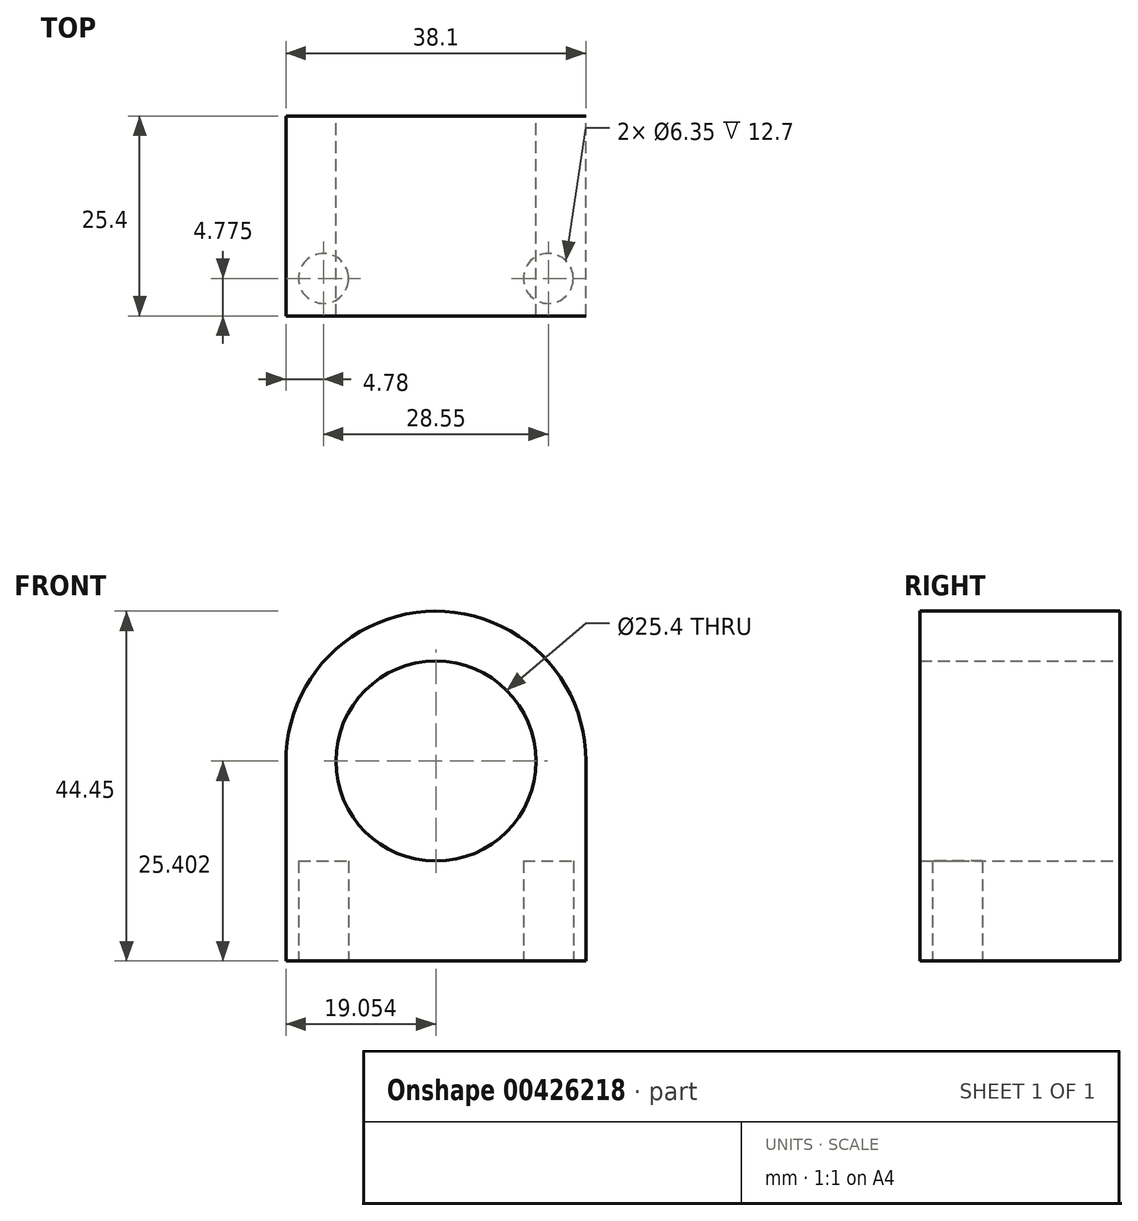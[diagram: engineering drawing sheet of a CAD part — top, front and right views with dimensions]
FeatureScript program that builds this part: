
annotation { "Feature Type Name" : "Feature", "Feature Type Description" : "" }
export const myFeature = defineFeature(function(context is Context, id is Id, definition is map)
    precondition{}
    {
        {
            var Q0;
            Q0=qCreatedBy(makeId("Front.planeOp"),FACE);
            var sketch = newSketch(context, id + "F0", { "sketchPlane" : qUnion([Q0])});
            skArc(sketch, "E0", {"start": v(4.83, 30.33) * mm, "mid": v(-14.3, 49.38) * mm, "end": v(-33.27, 30.17) * mm});
            skCircle(sketch, "E1", {"center": v(-14.22, 30.33) * mm, "radius": 12.7 * mm});
            skLineSegment(sketch, "E2", {"start": v(-33.27, 30.5) * mm, "end": v(-33.27, 4.93) * mm});
            skLineSegment(sketch, "E3", {"start": v(-33.27, 4.93) * mm, "end": v(4.83, 4.93) * mm});
            skLineSegment(sketch, "E4", {"start": v(4.83, 4.93) * mm, "end": v(4.83, 30.33) * mm});
            skSolve(sketch);
        }
        {
            var Q0;
            Q0 = qSketchRegion(id + "F0", true);
            extrude(context, id + "F1", {"entities" : qUnion([Q0]), "depth" : 25.4 * mm});
        }
        {
            var Q0;
            Q0=makeQuery(id+"F1.opExtrude","SWEPT_FACE",FACE,{"disambiguationData":[OSD([sQuery(id+"F0.wireOp",EDGE,"E3")])]});
            var sketch = newSketch(context, id + "F2", { "sketchPlane" : qUnion([Q0])});
            skCircle(sketch, "E5", {"center": v(-28.5, 20.62) * mm, "radius": 3.18 * mm});
            skCircle(sketch, "E6", {"center": v(0.06, 20.62) * mm, "radius": 3.18 * mm});
            skSolve(sketch);
        }
        {
            var Q0;
            Q0 = qSketchRegion(id + "F2", true);
            extrude(context, id + "F3", {"entities" : qUnion([Q0]), "operationType" : NewBodyOperationType.REMOVE, "oppositeDirection" : true, "depth" : 12.7 * mm});
        }
    });
